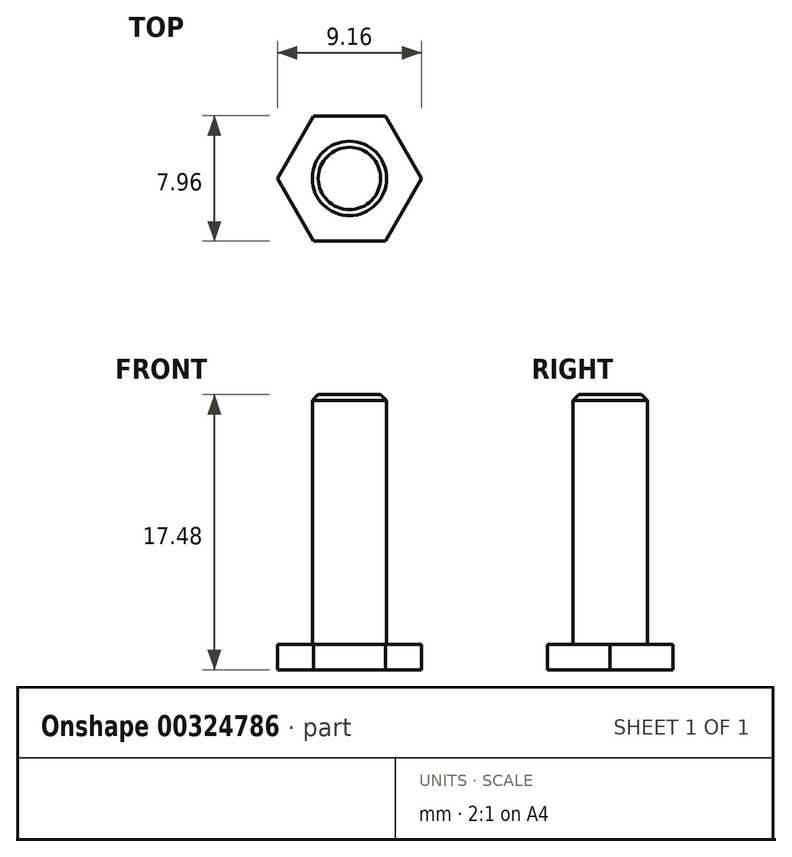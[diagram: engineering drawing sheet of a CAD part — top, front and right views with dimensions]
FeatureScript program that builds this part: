
annotation { "Feature Type Name" : "Feature", "Feature Type Description" : "" }
export const myFeature = defineFeature(function(context is Context, id is Id, definition is map)
    precondition{}
    {
        {
            var Q0;
            Q0=qCreatedBy(makeId("Top.planeOp"),FACE);
            var sketch = newSketch(context, id + "F0", { "sketchPlane" : qUnion([Q0])});
            skCircle(sketch, "E0", {"center": v(0, 0) * mm, "radius": 4.58 * mm, "construction": true});
            skLineSegment(sketch, "E1", {"start": v(-2.28, 3.98) * mm, "end": v(2.28, 3.98) * mm});
            skLineSegment(sketch, "E2", {"start": v(2.28, 3.98) * mm, "end": v(4.58, 0) * mm});
            skLineSegment(sketch, "E3", {"start": v(4.58, 0) * mm, "end": v(2.28, -3.98) * mm});
            skLineSegment(sketch, "E4", {"start": v(2.28, -3.98) * mm, "end": v(-2.28, -3.98) * mm});
            skLineSegment(sketch, "E5", {"start": v(-2.28, -3.98) * mm, "end": v(-4.58, 0) * mm});
            skLineSegment(sketch, "E6", {"start": v(-4.58, 0) * mm, "end": v(-2.28, 3.98) * mm});
            skSolve(sketch);
        }
        {
            var Q0;
            Q0=makeQuery(id+"F0.imprint","IMPRINT",FACE,{"disambiguationData":[TD([[makeQuery(id+"F0.imprint","IMPRINT",EDGE,{"derivedFrom":sQuery(id+"F0.wireOp",EDGE,"E1")}),-1.0]])]});
            extrude(context, id + "F1", {"entities" : qUnion([Q0]), "depth" : 1.6 * mm, "offsetDistance" : 25.4 * mm});
        }
        {
            var Q0;
            Q0=makeQuery(id+"F1.opExtrude","CAP_FACE",FACE,{"disambiguationData":[OSD([sQuery(id+"F0.wireOp",EDGE,"E1"),sQuery(id+"F0.wireOp",EDGE,"E2"),sQuery(id+"F0.wireOp",EDGE,"E3"),sQuery(id+"F0.wireOp",EDGE,"E4"),sQuery(id+"F0.wireOp",EDGE,"E5"),sQuery(id+"F0.wireOp",EDGE,"E6")])],"isStart":false});
            var sketch = newSketch(context, id + "F2", { "sketchPlane" : qUnion([Q0])});
            skCircle(sketch, "E7", {"center": v(0, 0) * mm, "radius": 2.36 * mm});
            skSolve(sketch);
        }
        {
            var Q0;
            Q0=makeQuery(id+"F2.imprint","IMPRINT",FACE,{"disambiguationData":[TD([[makeQuery(id+"F2.imprint","IMPRINT",EDGE,{"derivedFrom":sQuery(id+"F2.wireOp",EDGE,"E7")}),1.0]])]});
            extrude(context, id + "F3", {"entities" : qUnion([Q0]), "operationType" : NewBodyOperationType.ADD, "depth" : 15.88 * mm, "offsetDistance" : 25.4 * mm});
        }
        {
            var Q0;
            Q0=makeQuery(id+"F3.opExtrude","CAP_EDGE",EDGE,{"disambiguationData":[OSD([sQuery(id+"F2.wireOp",EDGE,"E7")])],"isStart":false});
            chamfer(context, id + "F4", {"entities" : qUnion([Q0]), "width" : 0.38 * mm, "tangentPropagation" : true});
        }
    });
